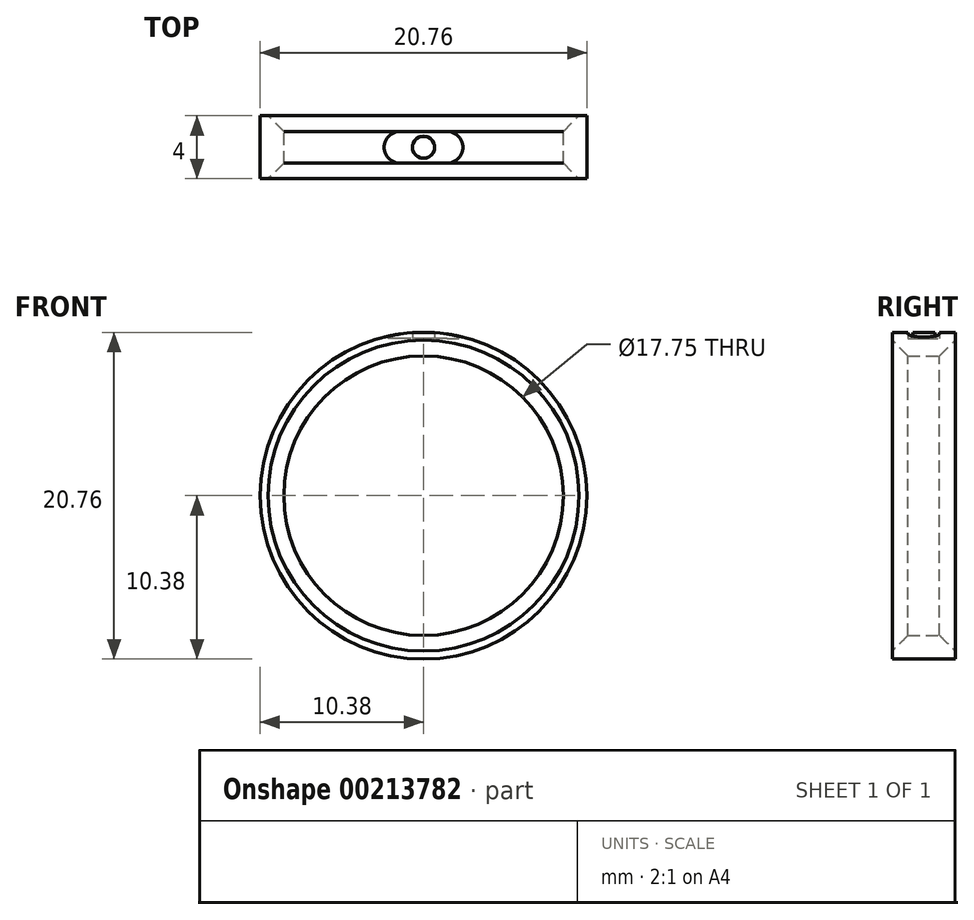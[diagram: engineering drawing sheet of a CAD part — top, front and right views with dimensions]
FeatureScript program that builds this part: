
annotation { "Feature Type Name" : "Feature", "Feature Type Description" : "" }
export const myFeature = defineFeature(function(context is Context, id is Id, definition is map)
    precondition{}
    {
        {
            var Q0;
            Q0=qCreatedBy(makeId("Front.planeOp"),FACE);
            var sketch = newSketch(context, id + "F0", { "sketchPlane" : qUnion([Q0])});
            skCircle(sketch, "E0", {"center": v(0, 0) * mm, "radius": 8.88 * mm});
            skCircle(sketch, "E1.0", {"center": v(0, 0) * mm, "radius": 10.38 * mm});
            skSolve(sketch);
        }
        {
            var Q0;
            Q0=makeQuery(id+"F0.imprint","IMPRINT",FACE,{"disambiguationData":[TD([[makeQuery(id+"F0.imprint","IMPRINT",EDGE,{"derivedFrom":sQuery(id+"F0.wireOp",EDGE,"E0")}),-1.0]])]});
            extrude(context, id + "F1", {"entities" : qUnion([Q0]), "depth" : 2 * mm, "hasSecondDirection" : true, "secondDirectionOppositeDirection" : true, "secondDirectionDepth" : 2 * mm});
        }
        {
            var Q0;
            Q0=makeQuery(id+"F1.opExtrude","CAP_EDGE",EDGE,{"disambiguationData":[OSD([sQuery(id+"F0.wireOp",EDGE,"E0")])],"isStart":false});
            var Q1;
            Q1=makeQuery(id+"F1.opExtrude","CAP_EDGE",EDGE,{"disambiguationData":[OSD([sQuery(id+"F0.wireOp",EDGE,"E0")])],"isStart":true});
            chamfer(context, id + "F2", {"entities" : qUnion([Q0, Q1]), "width" : 1 * mm, "tangentPropagation" : true});
        }
        {
            var Q0;
            Q0=qCreatedBy(makeId("Top.planeOp"),FACE);
            var sketch = newSketch(context, id + "F3", { "sketchPlane" : qUnion([Q0])});
            skLineSegment(sketch, "E2.bottom", {"start": v(1.5, -1) * mm, "end": v(-1.5, -1) * mm});
            skLineSegment(sketch, "E2.top", {"start": v(1.5, 1) * mm, "end": v(-1.5, 1) * mm});
            skLineSegment(sketch, "E2.left", {"start": v(2.5, 0) * mm, "end": v(2.5, 0) * mm});
            skLineSegment(sketch, "E2.right", {"start": v(-2.5, 0) * mm, "end": v(-2.5, 0) * mm});
            skPoint(sketch, "E2.middle", {"position": v(0, 0) * mm});
            skPoint(sketch, "E3.visualSharp", {"position": v(2.5, 1) * mm});
            skArc(sketch, "E3.filletArc", {"start": v(2.5, 0) * mm, "mid": v(2.2, 0.7) * mm, "end": v(1.5, 1) * mm});
            skPoint(sketch, "E4.visualSharp", {"position": v(2.5, -1) * mm});
            skArc(sketch, "E4.filletArc", {"start": v(1.5, -1) * mm, "mid": v(2.2, -0.7) * mm, "end": v(2.5, 0) * mm});
            skPoint(sketch, "E5.visualSharp", {"position": v(-2.5, -1) * mm});
            skArc(sketch, "E5.filletArc", {"start": v(-2.5, 0) * mm, "mid": v(-2.2, -0.7) * mm, "end": v(-1.5, -1) * mm});
            skPoint(sketch, "E6.visualSharp", {"position": v(-2.5, 1) * mm});
            skArc(sketch, "E6.filletArc", {"start": v(-1.5, 1) * mm, "mid": v(-2.2, 0.7) * mm, "end": v(-2.5, 0) * mm});
            skCircle(sketch, "E7", {"center": v(0, 0) * mm, "radius": 0.7 * mm});
            skSolve(sketch);
        }
        {
            var Q0;
            Q0=makeQuery(id+"F3.imprint","IMPRINT",FACE,{"disambiguationData":[TD([[makeQuery(id+"F3.imprint","IMPRINT",EDGE,{"derivedFrom":sQuery(id+"F3.wireOp",EDGE,"E2.bottom")}),-1.0]])]});
            extrude(context, id + "F4", {"entities" : qUnion([Q0]), "operationType" : NewBodyOperationType.REMOVE, "depth" : 25 * mm, "hasSecondDirection" : true, "secondDirectionOppositeDirection" : false, "secondDirectionDepth" : (17.75 / 2 + 1.1) * mm, "offsetDistance" : 25 * mm});
        }
    });
